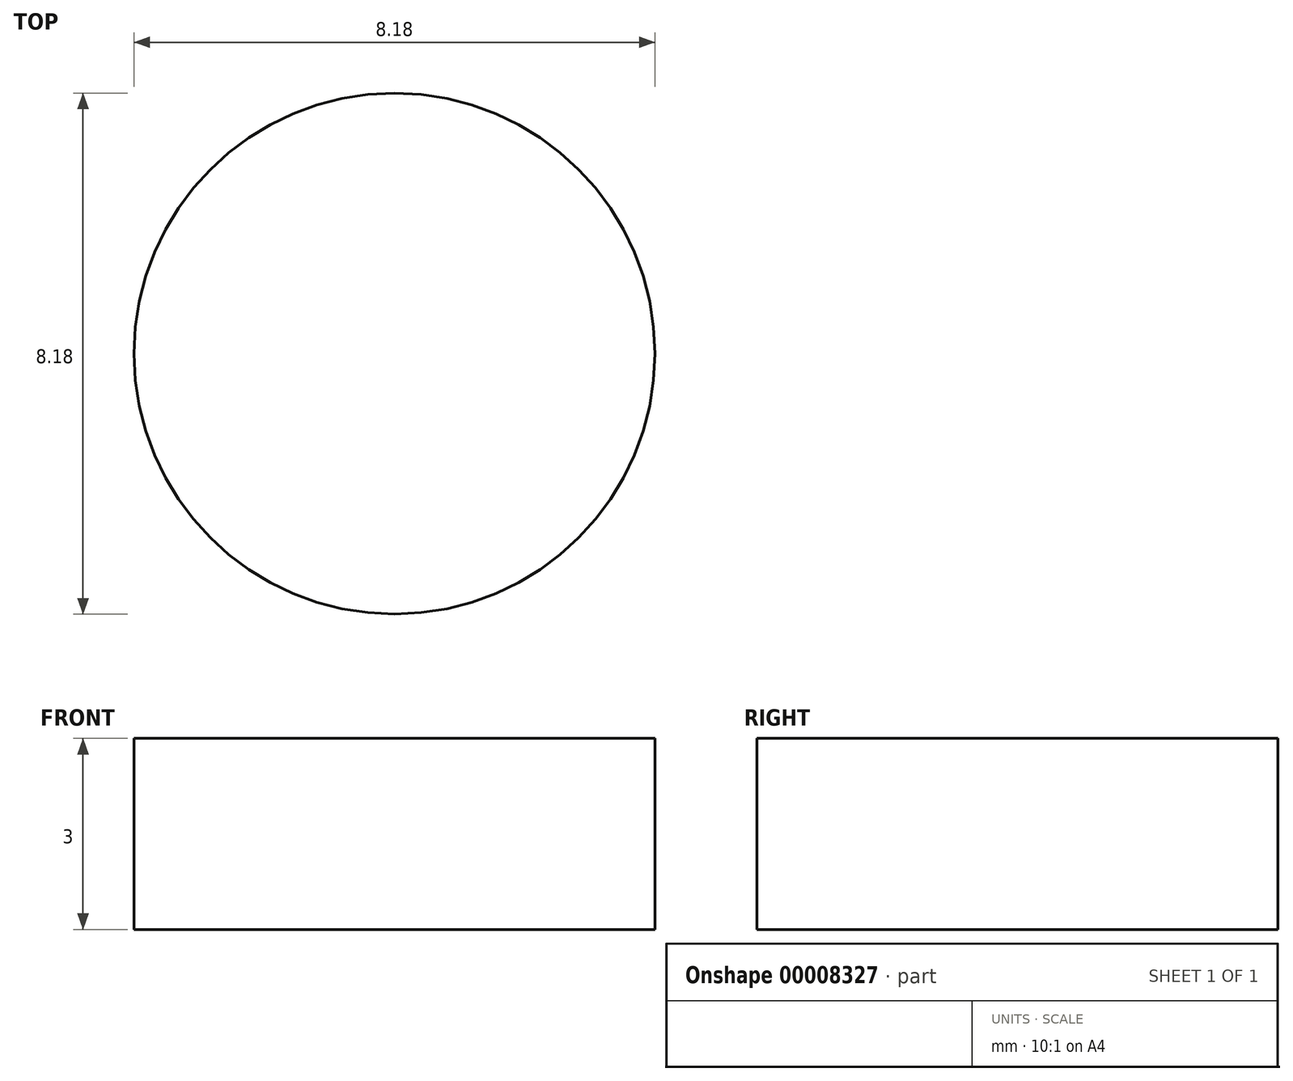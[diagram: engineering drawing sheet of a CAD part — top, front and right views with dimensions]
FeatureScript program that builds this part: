
annotation { "Feature Type Name" : "Feature", "Feature Type Description" : "" }
export const myFeature = defineFeature(function(context is Context, id is Id, definition is map)
    precondition{}
    {
        {
            var Q0;
            Q0=qCreatedBy(makeId("Top.planeOp"),FACE);
            var sketch = newSketch(context, id + "F0", { "sketchPlane" : qUnion([Q0])});
            skLineSegment(sketch, "E0.bottom", {"start": v(0, 0) * mm, "end": v(25, 0) * mm});
            skLineSegment(sketch, "E0.top", {"start": v(0, 12.5) * mm, "end": v(25, 12.5) * mm});
            skLineSegment(sketch, "E0.left", {"start": v(0, 0) * mm, "end": v(0, 12.5) * mm});
            skLineSegment(sketch, "E0.right", {"start": v(25, 0) * mm, "end": v(25, 12.5) * mm});
            skLineSegment(sketch, "E1.0.MirrorCS", {"start": v(25, 0) * mm, "end": v(25, -12.5) * mm});
            skLineSegment(sketch, "E1.1.MirrorCS", {"start": v(0, -12.5) * mm, "end": v(25, -12.5) * mm});
            skLineSegment(sketch, "E1.3.MirrorCS", {"start": v(0, 0) * mm, "end": v(0, -12.5) * mm});
            skArc(sketch, "E2", {"start": v(25, -12.5) * mm, "mid": v(37.5, 0) * mm, "end": v(25, 12.5) * mm});
            skLineSegment(sketch, "E3.0.MirrorCS", {"start": v(0, 0) * mm, "end": v(-25, 0) * mm});
            skArc(sketch, "E3.2.MirrorCS", {"start": v(-25, -12.5) * mm, "mid": v(-37.5, 0) * mm, "end": v(-25, 12.5) * mm});
            skLineSegment(sketch, "E3.3.MirrorCS", {"start": v(0, 0) * mm, "end": v(-25, 0) * mm});
            skLineSegment(sketch, "E3.5.MirrorCS", {"start": v(0, -12.5) * mm, "end": v(-25, -12.5) * mm});
            skLineSegment(sketch, "E3.6.MirrorCS", {"start": v(-25, 0) * mm, "end": v(-25, 12.5) * mm});
            skLineSegment(sketch, "E3.7.MirrorCS", {"start": v(0, 12.5) * mm, "end": v(-25, 12.5) * mm});
            skLineSegment(sketch, "E3.8.MirrorCS", {"start": v(-25, 0) * mm, "end": v(-25, -12.5) * mm});
            skSolve(sketch);
        }
        {
            var Q0;
            Q0=makeQuery(id+"F0.imprint","IMPRINT",FACE,{"disambiguationData":[TD([[makeQuery(id+"F0.imprint","IMPRINT",EDGE,{"derivedFrom":sQuery(id+"F0.wireOp",EDGE,"E3.3.MirrorCS")}),-1.0]])]});
            var Q1;
            Q1=makeQuery(id+"F0.imprint","IMPRINT",FACE,{"disambiguationData":[TD([[makeQuery(id+"F0.imprint","IMPRINT",EDGE,{"derivedFrom":sQuery(id+"F0.wireOp",EDGE,"E1.0.MirrorCS")}),-1.0]])]});
            var Q2;
            Q2=makeQuery(id+"F0.imprint","IMPRINT",FACE,{"disambiguationData":[TD([[makeQuery(id+"F0.imprint","IMPRINT",EDGE,{"derivedFrom":sQuery(id+"F0.wireOp",EDGE,"E1.3.MirrorCS")}),-1.0]])]});
            var Q3;
            Q3=makeQuery(id+"F0.imprint","IMPRINT",FACE,{"disambiguationData":[TD([[makeQuery(id+"F0.imprint","IMPRINT",EDGE,{"derivedFrom":sQuery(id+"F0.wireOp",EDGE,"E3.2.MirrorCS")}),-1.0]])]});
            var Q4;
            Q4=makeQuery(id+"F0.imprint","IMPRINT",FACE,{"disambiguationData":[TD([[makeQuery(id+"F0.imprint","IMPRINT",EDGE,{"derivedFrom":sQuery(id+"F0.wireOp",EDGE,"E0.top")}),-1.0]])]});
            var Q5;
            Q5=makeQuery(id+"F0.imprint","IMPRINT",FACE,{"disambiguationData":[TD([[makeQuery(id+"F0.imprint","IMPRINT",EDGE,{"derivedFrom":sQuery(id+"F0.wireOp",EDGE,"E0.right")}),-1.0]])]});
            extrude(context, id + "F1", {"entities" : qUnion([Q0, Q1, Q2, Q3, Q4, Q5]), "depth" : 3 * mm});
        }
        {
            var Q0;
            Q0=makeQuery(id+"F1.opExtrude","CAP_FACE",FACE,{"disambiguationData":[OSD([sQuery(id+"F0.wireOp",EDGE,"E0.top"),sQuery(id+"F0.wireOp",EDGE,"E1.1.MirrorCS"),sQuery(id+"F0.wireOp",EDGE,"E2"),sQuery(id+"F0.wireOp",EDGE,"E3.2.MirrorCS"),sQuery(id+"F0.wireOp",EDGE,"E3.5.MirrorCS"),sQuery(id+"F0.wireOp",EDGE,"E3.7.MirrorCS")])],"isStart":true});
            var sketch = newSketch(context, id + "F2", { "sketchPlane" : qUnion([Q0])});
            skCircle(sketch, "E4", {"center": v(-25, 0) * mm, "radius": 4.09 * mm});
            skCircle(sketch, "E5.0.MirrorC", {"center": v(25, 0) * mm, "radius": 4.09 * mm});
            skSolve(sketch);
        }
        {
            var Q0;
            Q0=makeQuery(id+"F2.imprint","IMPRINT",FACE,{"disambiguationData":[TD([[makeQuery(id+"F2.imprint","IMPRINT",EDGE,{"derivedFrom":sQuery(id+"F2.wireOp",EDGE,"E4")}),1.0]])]});
            var Q1;
            Q1=makeQuery(id+"F2.imprint","IMPRINT",FACE,{"disambiguationData":[TD([[makeQuery(id+"F2.imprint","IMPRINT",EDGE,{"derivedFrom":sQuery(id+"F2.wireOp",EDGE,"E5.0.MirrorC")}),-1.0]])]});
            extrude(context, id + "F3", {"entities" : qUnion([Q0, Q1]), "operationType" : NewBodyOperationType.REMOVE, "endBound" : BoundingType.THROUGH_ALL, "oppositeDirection" : true, "depth" : 25 * mm});
        }
    });
